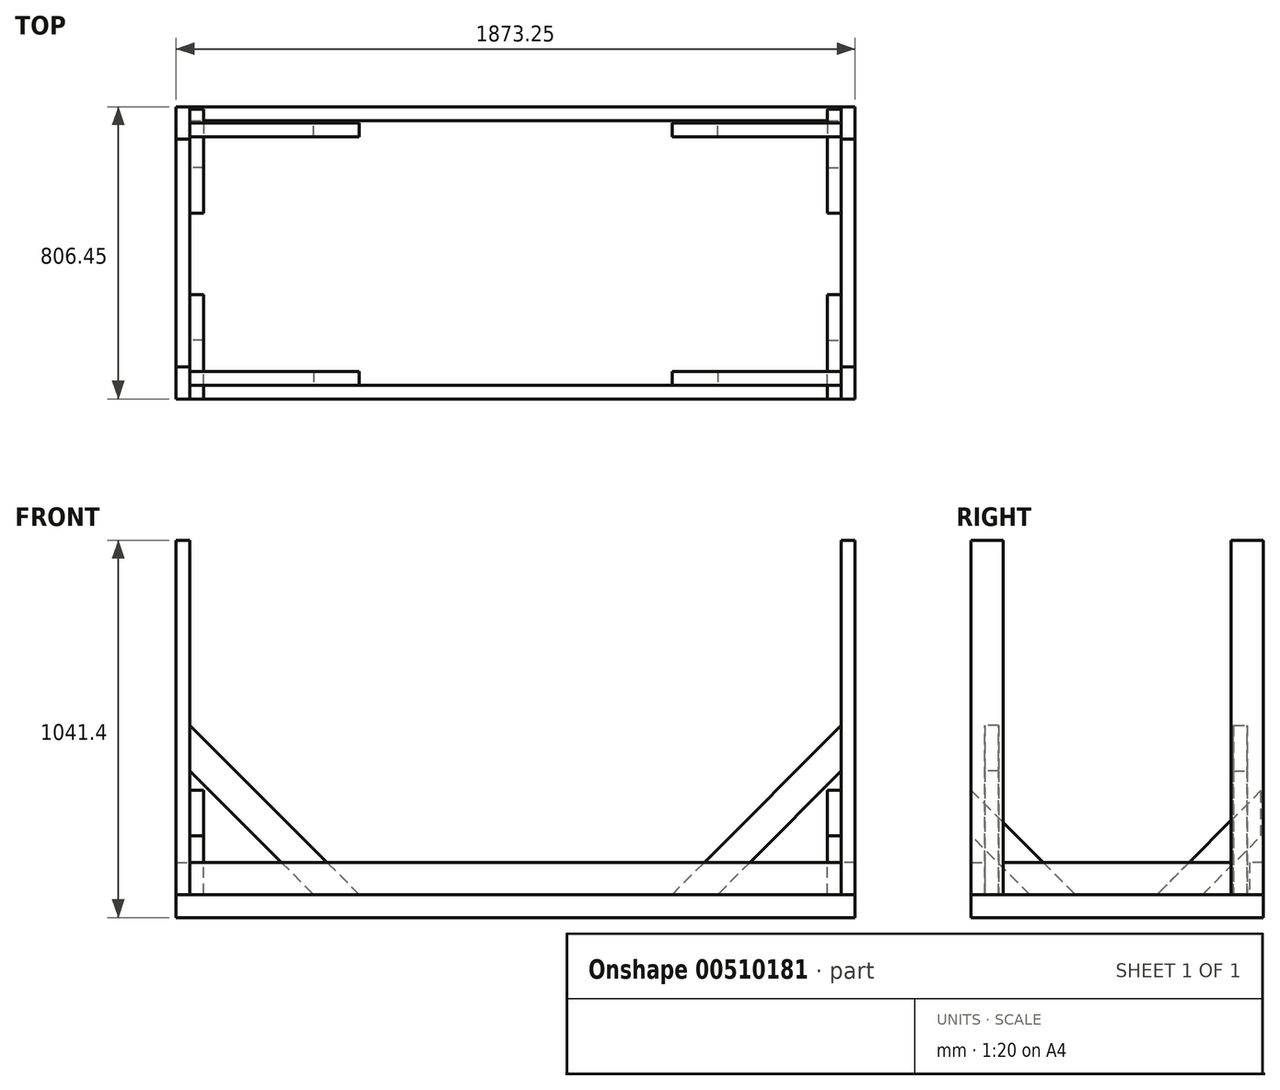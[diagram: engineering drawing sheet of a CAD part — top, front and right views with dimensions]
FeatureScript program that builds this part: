
annotation { "Feature Type Name" : "Feature", "Feature Type Description" : "" }
export const myFeature = defineFeature(function(context is Context, id is Id, definition is map)
    precondition{}
    {
        {
            var Q0;
            Q0=qCreatedBy(makeId("Top.planeOp"),FACE);
            var sketch = newSketch(context, id + "F0", { "sketchPlane" : qUnion([Q0])});
            skLineSegment(sketch, "E0.bottom", {"start": v(0, 0) * mm, "end": v(1873.25, 0) * mm});
            skLineSegment(sketch, "E0.top", {"start": v(0, 806.45) * mm, "end": v(1873.25, 806.45) * mm});
            skLineSegment(sketch, "E0.left", {"start": v(0, 0) * mm, "end": v(0, 806.45) * mm});
            skLineSegment(sketch, "E0.right", {"start": v(1873.25, 0) * mm, "end": v(1873.25, 806.45) * mm});
            skSolve(sketch);
        }
        {
            var Q0;
            Q0=makeQuery(id+"F0.imprint","IMPRINT",FACE,{"disambiguationData":[TD([[makeQuery(id+"F0.imprint","IMPRINT",EDGE,{"derivedFrom":sQuery(id+"F0.wireOp",EDGE,"E0.bottom")}),1.0]])]});
            extrude(context, id + "F1", {"entities" : qUnion([Q0]), "depth" : 63.5 * mm});
        }
        {
            var Q0;
            Q0=makeQuery(id+"F1.opExtrude","CAP_FACE",FACE,{"disambiguationData":[OSD([sQuery(id+"F0.wireOp",EDGE,"E0.bottom"),sQuery(id+"F0.wireOp",EDGE,"E0.top"),sQuery(id+"F0.wireOp",EDGE,"E0.left"),sQuery(id+"F0.wireOp",EDGE,"E0.right")])],"isStart":false});
            var sketch = newSketch(context, id + "F2", { "sketchPlane" : qUnion([Q0])});
            skLineSegment(sketch, "E1.bottom", {"start": v(0, 0) * mm, "end": v(38.1, 0) * mm});
            skLineSegment(sketch, "E1.top", {"start": v(0, 88.9) * mm, "end": v(38.1, 88.9) * mm});
            skLineSegment(sketch, "E1.left", {"start": v(0, 0) * mm, "end": v(0, 88.9) * mm});
            skLineSegment(sketch, "E1.right", {"start": v(38.1, 0) * mm, "end": v(38.1, 88.9) * mm});
            skLineSegment(sketch, "E2.bottom", {"start": v(1873.25, 0) * mm, "end": v(1835.15, 0) * mm});
            skLineSegment(sketch, "E2.top", {"start": v(1873.25, 88.9) * mm, "end": v(1835.15, 88.9) * mm});
            skLineSegment(sketch, "E2.left", {"start": v(1873.25, 0) * mm, "end": v(1873.25, 88.9) * mm});
            skLineSegment(sketch, "E2.right", {"start": v(1835.15, 0) * mm, "end": v(1835.15, 88.9) * mm});
            skLineSegment(sketch, "E3.bottom", {"start": v(1873.25, 806.45) * mm, "end": v(1835.15, 806.45) * mm});
            skLineSegment(sketch, "E3.top", {"start": v(1873.25, 717.55) * mm, "end": v(1835.15, 717.55) * mm});
            skLineSegment(sketch, "E3.left", {"start": v(1873.25, 806.45) * mm, "end": v(1873.25, 717.55) * mm});
            skLineSegment(sketch, "E3.right", {"start": v(1835.15, 806.45) * mm, "end": v(1835.15, 717.55) * mm});
            skLineSegment(sketch, "E4.bottom", {"start": v(0, 806.45) * mm, "end": v(38.1, 806.45) * mm});
            skLineSegment(sketch, "E4.top", {"start": v(0, 717.55) * mm, "end": v(38.1, 717.55) * mm});
            skLineSegment(sketch, "E4.left", {"start": v(0, 806.45) * mm, "end": v(0, 717.55) * mm});
            skLineSegment(sketch, "E4.right", {"start": v(38.1, 806.45) * mm, "end": v(38.1, 717.55) * mm});
            skSolve(sketch);
        }
        {
            var Q0;
            Q0=makeQuery(id+"F2.imprint","IMPRINT",FACE,{"disambiguationData":[TD([[makeQuery(id+"F2.imprint","IMPRINT",EDGE,{"derivedFrom":sQuery(id+"F2.wireOp",EDGE,"E4.bottom")}),-1.0]])]});
            var Q1;
            Q1=makeQuery(id+"F2.imprint","IMPRINT",FACE,{"disambiguationData":[TD([[makeQuery(id+"F2.imprint","IMPRINT",EDGE,{"derivedFrom":sQuery(id+"F2.wireOp",EDGE,"E1.bottom")}),1.0]])]});
            var Q2;
            Q2=makeQuery(id+"F2.imprint","IMPRINT",FACE,{"disambiguationData":[TD([[makeQuery(id+"F2.imprint","IMPRINT",EDGE,{"derivedFrom":sQuery(id+"F2.wireOp",EDGE,"E2.bottom")}),1.0]])]});
            var Q3;
            Q3=makeQuery(id+"F2.imprint","IMPRINT",FACE,{"disambiguationData":[TD([[makeQuery(id+"F2.imprint","IMPRINT",EDGE,{"derivedFrom":sQuery(id+"F2.wireOp",EDGE,"E3.bottom")}),-1.0]])]});
            extrude(context, id + "F3", {"entities" : qUnion([Q0, Q1, Q2, Q3]), "depth" : 977.9 * mm});
        }
        {
            var Q0;
            Q0=makeQuery(id+"F1.opExtrude","CAP_FACE",FACE,{"disambiguationData":[OSD([sQuery(id+"F0.wireOp",EDGE,"E0.bottom"),sQuery(id+"F0.wireOp",EDGE,"E0.top"),sQuery(id+"F0.wireOp",EDGE,"E0.left"),sQuery(id+"F0.wireOp",EDGE,"E0.right")])],"isStart":false});
            var sketch = newSketch(context, id + "F4", { "sketchPlane" : qUnion([Q0])});
            skLineSegment(sketch, "E5.bottom", {"start": v(38.1, 0) * mm, "end": v(1835.15, 0) * mm});
            skLineSegment(sketch, "E5.top", {"start": v(38.1, 38.1) * mm, "end": v(1835.15, 38.1) * mm});
            skLineSegment(sketch, "E5.left", {"start": v(38.1, 0) * mm, "end": v(38.1, 38.1) * mm});
            skLineSegment(sketch, "E5.right", {"start": v(1835.15, 0) * mm, "end": v(1835.15, 38.1) * mm});
            skLineSegment(sketch, "E6", {"start": v(0, 403.22) * mm, "end": v(1873.25, 403.23) * mm});
            skLineSegment(sketch, "E7.MirrorCS", {"start": v(38.1, 806.45) * mm, "end": v(1835.15, 806.45) * mm});
            skLineSegment(sketch, "E8.MirrorCS", {"start": v(38.1, 768.35) * mm, "end": v(1835.15, 768.35) * mm});
            skLineSegment(sketch, "E9.MirrorCS", {"start": v(1835.15, 806.45) * mm, "end": v(1835.15, 768.35) * mm});
            skLineSegment(sketch, "E10.MirrorCS", {"start": v(38.1, 806.45) * mm, "end": v(38.1, 768.35) * mm});
            skLineSegment(sketch, "E11.bottom", {"start": v(0, 717.55) * mm, "end": v(38.1, 717.55) * mm});
            skLineSegment(sketch, "E11.top", {"start": v(0, 88.9) * mm, "end": v(38.1, 88.9) * mm});
            skLineSegment(sketch, "E11.left", {"start": v(0, 717.55) * mm, "end": v(0, 88.9) * mm});
            skLineSegment(sketch, "E11.right", {"start": v(38.1, 717.55) * mm, "end": v(38.1, 88.9) * mm});
            skLineSegment(sketch, "E12", {"start": v(936.62, 768.35) * mm, "end": v(936.62, 38.1) * mm});
            skLineSegment(sketch, "E13.MirrorCS", {"start": v(1835.15, 717.55) * mm, "end": v(1835.15, 88.9) * mm});
            skLineSegment(sketch, "E14.MirrorCS", {"start": v(1873.25, 717.55) * mm, "end": v(1873.25, 88.9) * mm});
            skLineSegment(sketch, "E15.MirrorCS", {"start": v(1873.25, 717.55) * mm, "end": v(1835.15, 717.55) * mm});
            skLineSegment(sketch, "E16.MirrorCS", {"start": v(1873.25, 88.9) * mm, "end": v(1835.15, 88.9) * mm});
            skSolve(sketch);
        }
        {
            var Q0;
            {var subQ5=sQuery(id+"F4.wireOp",EDGE,"E11.bottom");Q0=makeQuery(id+"F4.imprint","IMPRINT",FACE,{"disambiguationData":[TD([[makeQuery(id+"F4.imprint","IMPRINT",EDGE,{"derivedFrom":subQ5}),-1.0]])]});}
            var Q1;
            {var subQ5=sQuery(id+"F4.wireOp",EDGE,"E11.top");Q1=makeQuery(id+"F4.imprint","IMPRINT",FACE,{"disambiguationData":[TD([[makeQuery(id+"F4.imprint","IMPRINT",EDGE,{"derivedFrom":subQ5}),1.0]])]});}
            var Q2;
            Q2=makeQuery(id+"F4.imprint","IMPRINT",FACE,{"disambiguationData":[TD([[makeQuery(id+"F4.imprint","IMPRINT",EDGE,{"derivedFrom":sQuery(id+"F4.wireOp",EDGE,"E5.bottom")}),1.0]])]});
            var Q3;
            Q3=makeQuery(id+"F4.imprint","IMPRINT",FACE,{"disambiguationData":[TD([[makeQuery(id+"F4.imprint","IMPRINT",EDGE,{"derivedFrom":sQuery(id+"F4.wireOp",EDGE,"E7.MirrorCS")}),-1.0]])]});
            var Q4;
            {var subQ5=sQuery(id+"F4.wireOp",EDGE,"E15.MirrorCS");Q4=makeQuery(id+"F4.imprint","IMPRINT",FACE,{"disambiguationData":[TD([[makeQuery(id+"F4.imprint","IMPRINT",EDGE,{"derivedFrom":subQ5}),1.0]])]});}
            var Q5;
            {var subQ5=sQuery(id+"F4.wireOp",EDGE,"E16.MirrorCS");Q5=makeQuery(id+"F4.imprint","IMPRINT",FACE,{"disambiguationData":[TD([[makeQuery(id+"F4.imprint","IMPRINT",EDGE,{"derivedFrom":subQ5}),-1.0]])]});}
            extrude(context, id + "F5", {"entities" : qUnion([Q0, Q1, Q2, Q3, Q4, Q5]), "depth" : 88.9 * mm});
        }
        {
            var Q0;
            Q0=makeQuery(id+"F5.opExtrude","SWEPT_FACE",FACE,{"disambiguationData":[OSD([sQuery(id+"F4.wireOp",EDGE,"E5.top")])]});
            var sketch = newSketch(context, id + "F6", { "sketchPlane" : qUnion([Q0])});
            skLineSegment(sketch, "E17", {"start": v(-505.07, 63.5) * mm, "end": v(-38.1, 530.47) * mm});
            skLineSegment(sketch, "E18", {"start": v(-38.1, 530.47) * mm, "end": v(-38.1, 404.75) * mm});
            skLineSegment(sketch, "E19", {"start": v(-38.1, 404.75) * mm, "end": v(-379.35, 63.5) * mm});
            skLineSegment(sketch, "E20", {"start": v(-379.35, 63.5) * mm, "end": v(-505.07, 63.5) * mm});
            skLineSegment(sketch, "E21", {"start": v(-936.63, 152.4) * mm, "end": v(-936.63, 63.5) * mm});
            skLineSegment(sketch, "E22.MirrorCS", {"start": v(-1368.18, 63.5) * mm, "end": v(-1835.15, 530.47) * mm});
            skLineSegment(sketch, "E23.MirrorCS", {"start": v(-1493.9, 63.5) * mm, "end": v(-1368.18, 63.5) * mm});
            skLineSegment(sketch, "E24.MirrorCS", {"start": v(-1835.15, 404.75) * mm, "end": v(-1493.9, 63.5) * mm});
            skLineSegment(sketch, "E25.MirrorCS", {"start": v(-1835.15, 530.47) * mm, "end": v(-1835.15, 404.75) * mm});
            skSolve(sketch);
        }
        {
            var Q0;
            {var subQ0=sQuery(id+"F6.wireOp",EDGE,"E18");Q0=makeQuery(id+"F6.imprint","IMPRINT",FACE,{"disambiguationData":[TD([[makeQuery(id+"F6.imprint","IMPRINT",EDGE,{"derivedFrom":subQ0}),-1.0]])]});}
            var Q1;
            {var subQ0=sQuery(id+"F6.wireOp",EDGE,"E20");Q1=makeQuery(id+"F6.imprint","IMPRINT",FACE,{"disambiguationData":[TD([[makeQuery(id+"F6.imprint","IMPRINT",EDGE,{"derivedFrom":subQ0}),-1.0]])]});}
            var Q2;
            {var subQ0=sQuery(id+"F6.wireOp",EDGE,"E25.MirrorCS");Q2=makeQuery(id+"F6.imprint","IMPRINT",FACE,{"disambiguationData":[TD([[makeQuery(id+"F6.imprint","IMPRINT",EDGE,{"derivedFrom":subQ0}),1.0]])]});}
            var Q3;
            {var subQ0=sQuery(id+"F6.wireOp",EDGE,"E23.MirrorCS");Q3=makeQuery(id+"F6.imprint","IMPRINT",FACE,{"disambiguationData":[TD([[makeQuery(id+"F6.imprint","IMPRINT",EDGE,{"derivedFrom":subQ0}),-1.0]])]});}
            extrude(context, id + "F7", {"entities" : qUnion([Q0, Q1, Q2, Q3]), "depth" : 38.1 * mm});
        }
        {
            var Q0;
            Q0=makeQuery(id+"F1.opExtrude","SWEPT_FACE",FACE,{"disambiguationData":[OSD([sQuery(id+"F0.wireOp",EDGE,"E0.bottom")])]});
            cPlane(context, id + "F8", {"entities" : qUnion([Q0]), "cplaneType" : CPlaneType.OFFSET, "offset" : 400.05 * mm, "oppositeDirection" : true, "width" : 152.4 * mm, "height" : 152.4 * mm});
        }
        {
            var Q0;
            Q0=makeQuery(id+"F7.opExtrude","SWEPT_BODY",BODY,{"disambiguationData":[OSD([sQuery(id+"F6.wireOp",EDGE,"E17"),sQuery(id+"F6.wireOp",EDGE,"E18"),sQuery(id+"F6.wireOp",EDGE,"E19"),sQuery(id+"F6.wireOp",EDGE,"E20")])]});
            var Q1;
            Q1=makeQuery(id+"F7.opExtrude","SWEPT_BODY",BODY,{"disambiguationData":[OSD([sQuery(id+"F6.wireOp",EDGE,"E22.MirrorCS"),sQuery(id+"F6.wireOp",EDGE,"E24.MirrorCS"),sQuery(id+"F6.wireOp",EDGE,"E25.MirrorCS"),sQuery(id+"F6.wireOp",EDGE,"E23.MirrorCS")])]});
            var Q2;
            Q2=qCreatedBy(id+"F8.planeOp",FACE);
            mirror(context, id + "F9", {"entities" : qUnion([Q0, Q1]), "mirrorPlane" : qUnion([Q2])});
        }
        {
            var Q0;
            Q0=makeQuery(id+"F5.opExtrude","SWEPT_FACE",FACE,{"disambiguationData":[OSD([sQuery(id+"F4.wireOp",EDGE,"E11.left")])]});
            cPlane(context, id + "F10", {"entities" : qUnion([Q0]), "cplaneType" : CPlaneType.OFFSET, "offset" : 936.62 * mm, "oppositeDirection" : true, "width" : 152.4 * mm, "height" : 152.4 * mm});
        }
        {
            var Q0;
            Q0=makeQuery(id+"F5.opExtrude","SWEPT_FACE",FACE,{"disambiguationData":[OSD([sQuery(id+"F4.wireOp",EDGE,"E11.right")])]});
            var sketch = newSketch(context, id + "F11", { "sketchPlane" : qUnion([Q0])});
            skLineSegment(sketch, "E26", {"start": v(161.64, 63.5) * mm, "end": v(0, 225.14) * mm});
            skLineSegment(sketch, "E27", {"start": v(0, 225.14) * mm, "end": v(0, 350.87) * mm});
            skLineSegment(sketch, "E28", {"start": v(0, 350.87) * mm, "end": v(287.37, 63.5) * mm});
            skLineSegment(sketch, "E29", {"start": v(287.37, 63.5) * mm, "end": v(161.64, 63.5) * mm});
            skSolve(sketch);
        }
        {
            var Q0;
            {var subQ0=sQuery(id+"F11.wireOp",EDGE,"E27");Q0=makeQuery(id+"F11.imprint","IMPRINT",FACE,{"disambiguationData":[TD([[makeQuery(id+"F11.imprint","IMPRINT",EDGE,{"derivedFrom":subQ0}),-1.0]])]});}
            var Q1;
            {var subQ0=sQuery(id+"F11.wireOp",EDGE,"E29");Q1=makeQuery(id+"F11.imprint","IMPRINT",FACE,{"disambiguationData":[TD([[makeQuery(id+"F11.imprint","IMPRINT",EDGE,{"derivedFrom":subQ0}),-1.0]])]});}
            extrude(context, id + "F12", {"entities" : qUnion([Q0, Q1]), "depth" : 38.1 * mm});
        }
        {
            var Q0;
            Q0=makeQuery(id+"F12.opExtrude","SWEPT_BODY",BODY,{"disambiguationData":[OSD([sQuery(id+"F11.wireOp",EDGE,"E26"),sQuery(id+"F11.wireOp",EDGE,"E27"),sQuery(id+"F11.wireOp",EDGE,"E28"),sQuery(id+"F11.wireOp",EDGE,"E29")])]});
            var Q1;
            Q1=qCreatedBy(id+"F8.planeOp",FACE);
            mirror(context, id + "F13", {"entities" : qUnion([Q0]), "mirrorPlane" : qUnion([Q1])});
        }
        {
            var Q0;
            Q0=makeQuery(id+"F12.opExtrude","SWEPT_BODY",BODY,{"disambiguationData":[OSD([sQuery(id+"F11.wireOp",EDGE,"E26"),sQuery(id+"F11.wireOp",EDGE,"E27"),sQuery(id+"F11.wireOp",EDGE,"E28"),sQuery(id+"F11.wireOp",EDGE,"E29")])]});
            var Q1;
            Q1=makeQuery(id+"F13.opPattern","COPY",BODY,{"derivedFrom":makeQuery(id+"F12.opExtrude","SWEPT_BODY",BODY,{"disambiguationData":[OSD([sQuery(id+"F11.wireOp",EDGE,"E26"),sQuery(id+"F11.wireOp",EDGE,"E27"),sQuery(id+"F11.wireOp",EDGE,"E28"),sQuery(id+"F11.wireOp",EDGE,"E29")])]}),"instanceName":"1"});
            var Q2;
            Q2=qCreatedBy(id+"F10.planeOp",FACE);
            mirror(context, id + "F14", {"entities" : qUnion([Q0, Q1]), "mirrorPlane" : qUnion([Q2])});
        }
    });
